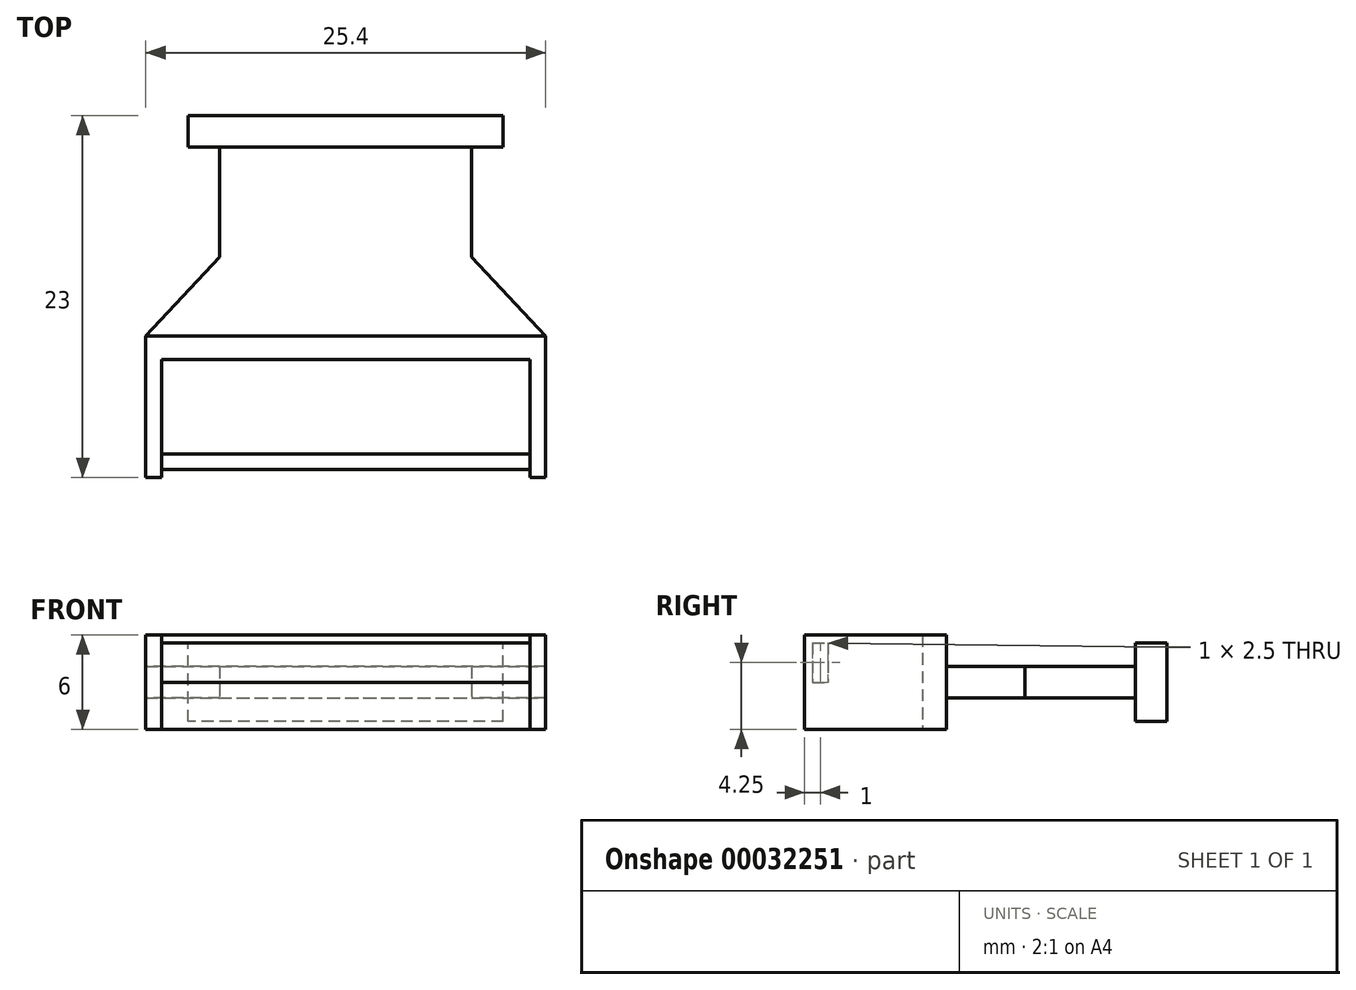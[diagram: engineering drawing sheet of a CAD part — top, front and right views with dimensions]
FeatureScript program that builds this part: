
annotation { "Feature Type Name" : "Feature", "Feature Type Description" : "" }
export const myFeature = defineFeature(function(context is Context, id is Id, definition is map)
    precondition{}
    {
        {
            var Q0;
            Q0=qCreatedBy(makeId("Front.planeOp"),FACE);
            var sketch = newSketch(context, id + "F0", { "sketchPlane" : qUnion([Q0])});
            skLineSegment(sketch, "E0.rect.bottom", {"start": v(10, -2.5) * mm, "end": v(-10, -2.5) * mm});
            skLineSegment(sketch, "E0.rect.top", {"start": v(10, 2.5) * mm, "end": v(-10, 2.5) * mm});
            skLineSegment(sketch, "E0.rect.left", {"start": v(10, -2.5) * mm, "end": v(10, 2.5) * mm});
            skLineSegment(sketch, "E0.rect.right", {"start": v(-10, -2.5) * mm, "end": v(-10, 2.5) * mm});
            skPoint(sketch, "E0.rect.middle", {"position": v(0, 0) * mm});
            skSolve(sketch);
        }
        {
            var Q0;
            Q0 = qSketchRegion(id + "F0", true);
            extrude(context, id + "F1", {"entities" : qUnion([Q0]), "depth" : 2 * mm});
        }
        {
            var Q0;
            Q0=makeQuery(id+"F1.opExtrude","CAP_FACE",FACE,{"disambiguationData":[OSD([sQuery(id+"F0.wireOp",EDGE,"E0.rect.bottom"),sQuery(id+"F0.wireOp",EDGE,"E0.rect.top"),sQuery(id+"F0.wireOp",EDGE,"E0.rect.left"),sQuery(id+"F0.wireOp",EDGE,"E0.rect.right")])],"isStart":false});
            var sketch = newSketch(context, id + "F2", { "sketchPlane" : qUnion([Q0])});
            skLineSegment(sketch, "E1.bottom", {"start": v(-8, 1) * mm, "end": v(8, 1) * mm});
            skLineSegment(sketch, "E1.top", {"start": v(-8, -1) * mm, "end": v(8, -1) * mm});
            skLineSegment(sketch, "E1.left", {"start": v(-8, 1) * mm, "end": v(-8, -1) * mm});
            skLineSegment(sketch, "E1.right", {"start": v(8, 1) * mm, "end": v(8, -1) * mm});
            skSolve(sketch);
        }
        {
            var Q0;
            Q0 = qSketchRegion(id + "F2", true);
            extrude(context, id + "F3", {"entities" : qUnion([Q0]), "operationType" : NewBodyOperationType.ADD, "depth" : 7 * mm});
        }
        {
            var Q0;
            Q0=makeQuery(id+"F3.opExtrude","SWEPT_FACE",FACE,{"disambiguationData":[OSD([sQuery(id+"F2.wireOp",EDGE,"E1.bottom")])]});
            var sketch = newSketch(context, id + "F4", { "sketchPlane" : qUnion([Q0])});
            skLineSegment(sketch, "E2", {"start": v(8, -9) * mm, "end": v(12.7, -14) * mm});
            skLineSegment(sketch, "E3", {"start": v(12.7, -14) * mm, "end": v(-12.7, -14) * mm});
            skLineSegment(sketch, "E4", {"start": v(-12.7, -14) * mm, "end": v(-8, -9) * mm});
            skLineSegment(sketch, "E5", {"start": v(-8, -9) * mm, "end": v(8, -9) * mm});
            skSolve(sketch);
        }
        {
            var Q0;
            Q0 = qSketchRegion(id + "F4", true);
            var Q1;
            Q1=makeQuery(id+"F3.opExtrude","SWEPT_FACE",FACE,{"disambiguationData":[OSD([sQuery(id+"F2.wireOp",EDGE,"E1.top")])]});
            extrude(context, id + "F5", {"entities" : qUnion([Q0]), "operationType" : NewBodyOperationType.ADD, "endBound" : BoundingType.UP_TO_SURFACE, "oppositeDirection" : true, "endBoundEntityFace" : qUnion([Q1]), "depth" : 25 * mm});
        }
        {
            var Q0;
            Q0=makeQuery(id+"F5.opExtrude","SWEPT_FACE",FACE,{"disambiguationData":[OSD([sQuery(id+"F4.wireOp",EDGE,"E3")])]});
            var sketch = newSketch(context, id + "F6", { "sketchPlane" : qUnion([Q0])});
            skLineSegment(sketch, "E6.bottom", {"start": v(-12.7, 3) * mm, "end": v(12.7, 3) * mm});
            skLineSegment(sketch, "E6.top", {"start": v(-12.7, -3) * mm, "end": v(12.7, -3) * mm});
            skLineSegment(sketch, "E6.left", {"start": v(-12.7, 3) * mm, "end": v(-12.7, -3) * mm});
            skLineSegment(sketch, "E6.right", {"start": v(12.7, 3) * mm, "end": v(12.7, -3) * mm});
            skSolve(sketch);
        }
        {
            var Q0;
            Q0 = qSketchRegion(id + "F6", true);
            extrude(context, id + "F7", {"entities" : qUnion([Q0]), "operationType" : NewBodyOperationType.ADD, "depth" : 1.5 * mm});
        }
        {
            var Q0;
            Q0=makeQuery(id+"F7.opExtrude","CAP_FACE",FACE,{"disambiguationData":[OSD([sQuery(id+"F6.wireOp",EDGE,"E6.bottom"),sQuery(id+"F6.wireOp",EDGE,"E6.top"),sQuery(id+"F6.wireOp",EDGE,"E6.left"),sQuery(id+"F6.wireOp",EDGE,"E6.right")])],"isStart":false});
            var sketch = newSketch(context, id + "F8", { "sketchPlane" : qUnion([Q0])});
            skLineSegment(sketch, "E7.bottom", {"start": v(-12.7, 3) * mm, "end": v(-11.7, 3) * mm});
            skLineSegment(sketch, "E7.top", {"start": v(-12.7, -3) * mm, "end": v(-11.7, -3) * mm});
            skLineSegment(sketch, "E7.left", {"start": v(-12.7, 3) * mm, "end": v(-12.7, -3) * mm});
            skLineSegment(sketch, "E7.right", {"start": v(-11.7, 3) * mm, "end": v(-11.7, -3) * mm});
            skLineSegment(sketch, "E8.bottom", {"start": v(12.7, 3) * mm, "end": v(11.7, 3) * mm});
            skLineSegment(sketch, "E8.top", {"start": v(12.7, -3) * mm, "end": v(11.7, -3) * mm});
            skLineSegment(sketch, "E8.left", {"start": v(12.7, 3) * mm, "end": v(12.7, -3) * mm});
            skLineSegment(sketch, "E8.right", {"start": v(11.7, 3) * mm, "end": v(11.7, -3) * mm});
            skSolve(sketch);
        }
        {
            var Q0;
            Q0 = qSketchRegion(id + "F8", true);
            extrude(context, id + "F9", {"entities" : qUnion([Q0]), "operationType" : NewBodyOperationType.ADD, "depth" : 7.5 * mm});
        }
        {
            var Q0;
            Q0=makeQuery(id+"F9.opExtrude","SWEPT_FACE",FACE,{"disambiguationData":[OSD([sQuery(id+"F8.wireOp",EDGE,"E7.right")])]});
            var sketch = newSketch(context, id + "F10", { "sketchPlane" : qUnion([Q0])});
            skLineSegment(sketch, "E9.bottom", {"start": v(-22.5, 2.5) * mm, "end": v(-21.5, 2.5) * mm});
            skLineSegment(sketch, "E9.top", {"start": v(-22.5, 0) * mm, "end": v(-21.5, 0) * mm});
            skLineSegment(sketch, "E9.left", {"start": v(-22.5, 2.5) * mm, "end": v(-22.5, 0) * mm});
            skLineSegment(sketch, "E9.right", {"start": v(-21.5, 2.5) * mm, "end": v(-21.5, 0) * mm});
            skSolve(sketch);
        }
        {
            var Q0;
            Q0=makeQuery(id+"F10.imprint","IMPRINT",FACE,{"disambiguationData":[TD([[makeQuery(id+"F10.imprint","IMPRINT",EDGE,{"derivedFrom":sQuery(id+"F10.wireOp",EDGE,"E9.bottom")}),-1.0]])]});
            var Q1;
            Q1=makeQuery(id+"F9.opExtrude","SWEPT_FACE",FACE,{"disambiguationData":[OSD([sQuery(id+"F8.wireOp",EDGE,"E8.right")])]});
            extrude(context, id + "F11", {"entities" : qUnion([Q0]), "operationType" : NewBodyOperationType.ADD, "endBound" : BoundingType.UP_TO_SURFACE, "endBoundEntityFace" : qUnion([Q1]), "depth" : 25 * mm});
        }
    });
